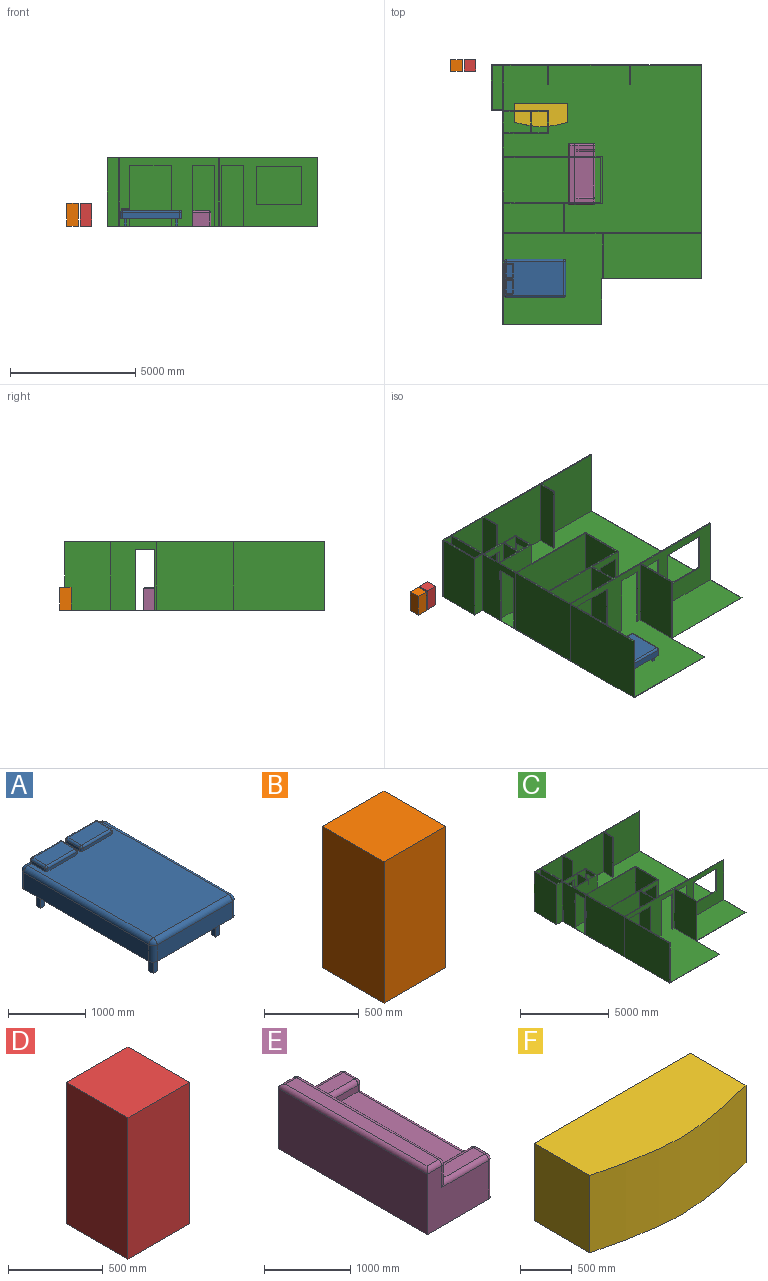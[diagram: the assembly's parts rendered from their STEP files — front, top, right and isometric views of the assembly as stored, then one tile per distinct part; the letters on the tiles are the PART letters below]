
ASSEMBLY  parts=6 mates=7
PART A: 74 faces, bbox 1524x2438.4x716.3 mm
  f0: plane 2286x1371.6mm, normal (0,0,1), area 2817151mm2, adj f9,f10,f14,f15,f39,f40,f42,f46
  f1: plane 1371.6x259.08mm, normal (0,1,0), area 355354.1mm2, adj f5,f8,f14,f17
  f2: plane 2286x259.08mm, normal (-1,0,0), area 592256.9mm2, adj f5,f11,f15,f17
  f3: plane 1371.6x259.08mm, normal (0,-1,0), area 355354.1mm2, adj f5,f6,f10,f11
  f4: plane 2286x259.08mm, normal (1,0,0), area 592256.9mm2, adj f5,f6,f8,f9
  f5: plane 2438.4x1524mm, normal (0,0,-1), area 3687911.5mm2, adj f1,f2,f3,f4,f6,f8,f11,f17
  f6: cylinder r=76.2mm len=259.08mm, axis (0,0,1), area 31010.5mm2, adj f3,f4,f5,f7
  f7: sphere r=76.2mm, area 9120.7mm2, adj f6,f9,f10
  f8: cylinder r=76.2mm len=259.08mm, axis (0,0,-1), area 31010.5mm2, adj f1,f4,f5,f12
  f9: cylinder r=76.2mm len=2286mm, axis (0,-1,0), area 273622mm2, adj f0,f4,f7,f12
  f10: cylinder r=76.2mm len=1371.6mm, axis (-1,0,0), area 164173.2mm2, adj f0,f3,f7,f13
  f11: cylinder r=76.2mm len=259.08mm, axis (0,0,-1), area 31010.5mm2, adj f2,f3,f5,f13
  f12: sphere r=76.2mm, area 9120.7mm2, adj f8,f9,f14
  f13: sphere r=76.2mm, area 9120.7mm2, adj f10,f11,f15
  f14: cylinder r=76.2mm len=1371.6mm, axis (1,0,0), area 164173.2mm2, adj f0,f1,f12,f16,f38,f44
  f15: cylinder r=76.2mm len=2286mm, axis (0,1,0), area 273622mm2, adj f0,f2,f13,f16
  f16: sphere r=76.2mm, area 9120.7mm2, adj f14,f15,f17
  f17: cylinder r=76.2mm len=259.08mm, axis (0,0,1), area 31010.5mm2, adj f1,f2,f5,f16
  f18: plane 304.8x76.2mm, normal (0,-1,0), area 23225.8mm2, adj f5,f19,f21,f22
  f19: plane 304.8x76.2mm, normal (-1,0,0), area 23225.8mm2, adj f5,f18,f20,f22
  f20: plane 304.8x76.2mm, normal (0,1,0), area 23225.8mm2, adj f5,f19,f21,f22
  f21: plane 304.8x76.2mm, normal (1,0,0), area 23225.8mm2, adj f5,f18,f20,f22
  f22: plane 76.2x76.2mm, normal (0,0,-1), area 5806.4mm2, adj f18,f19,f20,f21
  f23: plane 304.8x76.2mm, normal (0,-1,0), area 23225.8mm2, adj f5,f24,f26,f27
  f24: plane 304.8x76.2mm, normal (-1,0,0), area 23225.8mm2, adj f5,f23,f25,f27
  f25: plane 304.8x76.2mm, normal (0,1,0), area 23225.8mm2, adj f5,f24,f26,f27
  f26: plane 304.8x76.2mm, normal (1,0,0), area 23225.8mm2, adj f5,f23,f25,f27
  f27: plane 76.2x76.2mm, normal (0,0,-1), area 5806.4mm2, adj f23,f24,f25,f26
  f28: plane 304.8x76.2mm, normal (1,0,0), area 23225.8mm2, adj f5,f29,f31,f32
  f29: plane 304.8x76.2mm, normal (0,-1,0), area 23225.8mm2, adj f5,f28,f30,f32
  f30: plane 304.8x76.2mm, normal (-1,0,0), area 23225.8mm2, adj f5,f29,f31,f32
  f31: plane 304.8x76.2mm, normal (0,1,0), area 23225.8mm2, adj f5,f28,f30,f32
  f32: plane 76.2x76.2mm, normal (0,0,-1), area 5806.4mm2, adj f28,f29,f30,f31
  f33: plane 304.8x76.2mm, normal (0,-1,0), area 23225.8mm2, adj f5,f34,f36,f37
  f34: plane 304.8x76.2mm, normal (-1,0,0), area 23225.8mm2, adj f5,f33,f35,f37
  f35: plane 304.8x76.2mm, normal (0,1,0), area 23225.8mm2, adj f5,f34,f36,f37
  f36: plane 304.8x76.2mm, normal (1,0,0), area 23225.8mm2, adj f5,f33,f35,f37
  f37: plane 76.2x76.2mm, normal (0,0,-1), area 5806.4mm2, adj f33,f34,f35,f36
  f38: plane 579.07x29.28mm, normal (0,0,-1), area 16555mm2, adj f14,f41,f62,f67
  f39: plane 518.16x45.72mm, normal (0,-1,0), area 23690.3mm2, adj f0,f64,f70,f73
  f40: plane 243.84x45.72mm, normal (1,0,0), area 11148.4mm2, adj f0,f67,f71,f73
  f41: plane 518.16x45.72mm, normal (0,1,0), area 23690.3mm2, adj f38,f62,f66,f67
  f42: plane 243.84x45.72mm, normal (-1,0,0), area 11148.4mm2, adj f0,f62,f64,f65
  f43: plane 518.16x243.84mm, normal (0,0,1), area 126348.1mm2, adj f65,f66,f70,f71
  f44: plane 579.07x29.28mm, normal (0,0,-1), area 16555mm2, adj f14,f45,f52,f61
  f45: plane 518.16x45.72mm, normal (0,1,0), area 23690.3mm2, adj f44,f52,f58,f61
  f46: plane 243.84x45.72mm, normal (-1,0,0), area 11148.4mm2, adj f0,f55,f59,f61
  f47: plane 518.16x45.72mm, normal (0,-1,0), area 23690.3mm2, adj f0,f50,f54,f55
  f48: plane 243.84x45.72mm, normal (1,0,0), area 11148.4mm2, adj f0,f50,f52,f53
  f49: plane 518.16x243.84mm, normal (0,0,1), area 126348.1mm2, adj f53,f54,f58,f59
  f50: cylinder r=30.48mm len=45.72mm, axis (0,0,1), area 2189mm2, adj f0,f47,f48,f51
  f51: sphere r=30.48mm, area 1459.3mm2, adj f50,f53,f54
  f52: cylinder r=30.48mm len=45.72mm, axis (0,0,-1), area 2189mm2, adj f0,f44,f45,f48,f56
  f53: cylinder r=30.48mm len=243.84mm, axis (0,-1,0), area 11674.5mm2, adj f48,f49,f51,f56
  f54: cylinder r=30.48mm len=518.16mm, axis (-1,0,0), area 24808.4mm2, adj f47,f49,f51,f57
  f55: cylinder r=30.48mm len=45.72mm, axis (0,0,-1), area 2189mm2, adj f0,f46,f47,f57
  f56: sphere r=30.48mm, area 1459.3mm2, adj f52,f53,f58
  f57: sphere r=30.48mm, area 1459.3mm2, adj f54,f55,f59
  f58: cylinder r=30.48mm len=518.16mm, axis (1,0,0), area 24808.4mm2, adj f45,f49,f56,f60
  f59: cylinder r=30.48mm len=243.84mm, axis (0,1,0), area 11674.5mm2, adj f46,f49,f57,f60
  f60: sphere r=30.48mm, area 1459.3mm2, adj f58,f59,f61
  f61: cylinder r=30.48mm len=45.72mm, axis (0,0,1), area 2189mm2, adj f0,f44,f45,f46,f60
  f62: cylinder r=30.48mm len=45.72mm, axis (0,0,1), area 2189mm2, adj f0,f38,f41,f42,f63
  f63: sphere r=30.48mm, area 1459.3mm2, adj f62,f65,f66
  f64: cylinder r=30.48mm len=45.72mm, axis (0,0,-1), area 2189mm2, adj f0,f39,f42,f68
  f65: cylinder r=30.48mm len=243.84mm, axis (0,1,0), area 11674.5mm2, adj f42,f43,f63,f68
  f66: cylinder r=30.48mm len=518.16mm, axis (1,0,0), area 24808.4mm2, adj f41,f43,f63,f69
  f67: cylinder r=30.48mm len=45.72mm, axis (0,0,-1), area 2189mm2, adj f0,f38,f40,f41,f69
  f68: sphere r=30.48mm, area 1459.3mm2, adj f64,f65,f70
  f69: sphere r=30.48mm, area 1459.3mm2, adj f66,f67,f71
  f70: cylinder r=30.48mm len=518.16mm, axis (-1,0,0), area 24808.4mm2, adj f39,f43,f68,f72
  f71: cylinder r=30.48mm len=243.84mm, axis (0,-1,0), area 11674.5mm2, adj f40,f43,f69,f72
  f72: sphere r=30.48mm, area 1459.3mm2, adj f70,f71,f73
  f73: cylinder r=30.48mm len=45.72mm, axis (0,0,1), area 2189mm2, adj f0,f39,f40,f72
PART B: 6 faces, bbox 457.2x457.2x914.4 mm
  f0: plane 914.4x457.2mm, normal (0,-1,0), area 418063.7mm2, adj f1,f3,f4,f5
  f1: plane 914.4x457.2mm, normal (1,0,0), area 418063.7mm2, adj f0,f2,f4,f5
  f2: plane 914.4x457.2mm, normal (0,1,0), area 418063.7mm2, adj f1,f3,f4,f5
  f3: plane 914.4x457.2mm, normal (-1,0,0), area 418063.7mm2, adj f0,f2,f4,f5
  f4: plane 457.2x457.2mm, normal (0,0,1), area 209031.8mm2, adj f0,f1,f2,f3
  f5: plane 457.2x457.2mm, normal (0,0,-1), area 209031.8mm2, adj f0,f1,f2,f3
PART C: 85 faces, bbox 8382x10363.2x2750.8 mm
  f0: plane 3915.35x2743.2mm, normal (0,-1,0), area 5798149.8mm2, adj f2,f10,f19,f23,f78,f79,f80,f81
  f1: plane 3093.72x1.33mm, normal (0,0,1), area 4110.8mm2, adj f14,f17,f71,f73
  f2: plane 10324.82x7924.8mm, normal (0,0,1), area 73158988.7mm2, adj f0,f3,f4,f5,f6,f7,f8,f9
  f3: plane 3918.01x2743.2mm, normal (0,1,0), area 10747881.6mm2, adj f2,f16,f23,f72
  f4: plane 2743.2x1790.42mm, normal (1,0,0), area 4911492.8mm2, adj f2,f5,f23,f62
  f5: plane 2743.2x1783.08mm, normal (0,1,0), area 3033284.3mm2, adj f2,f4,f23,f42,f54,f55,f56
  f6: plane 3918.01x2743.2mm, normal (0,-1,0), area 4504797.3mm2, adj f2,f18,f23,f35,f36,f37,f38,f39
  f7: plane 3962.4x2750.82mm, normal (0,-1,0), area 155612.6mm2, adj f2,f8,f14,f15,f23,f74
  f8: plane 1828.8x7.62mm, normal (1,0,0), area 13935.5mm2, adj f2,f7,f9,f15
  f9: plane 3962.4x2750.82mm, normal (0,-1,0), area 155612.6mm2, adj f2,f8,f10,f15,f18,f19,f23
  f10: plane 8534.4x2750.82mm, normal (1,0,0), area 295722.6mm2, adj f0,f2,f9,f11,f15,f20,f23,f70
  f11: plane 8382x2750.82mm, normal (0,1,0), area 23057373.2mm2, adj f10,f12,f15,f23
  f12: plane 2750.82x1828.8mm, normal (-1,0,0), area 5030699.6mm2, adj f11,f13,f15,f23
  f13: plane 2750.82x457.2mm, normal (0,-1,0), area 1257674.9mm2, adj f12,f14,f15,f23
  f14: plane 8534.4x2750.82mm, normal (-1,0,0), area 13131844.7mm2, adj f1,f2,f7,f13,f15,f23,f71,f73
  f15: plane 10363.2x8382mm, normal (0,0,-1), area 75715977.6mm2, adj f7,f8,f9,f10,f11,f12,f13,f14
  f16: plane 2743.2x1874.52mm, normal (1,0,0), area 5142183.3mm2, adj f2,f3,f22,f23
  f17: plane 3093.72x2743.2mm, normal (-1,0,0), area 8486692.7mm2, adj f1,f23,f71,f73
  f18: plane 2743.2x1783.08mm, normal (-1,0,0), area 4891345.1mm2, adj f2,f6,f9,f23
  f19: plane 2743.2x1783.08mm, normal (1,0,0), area 4891345.1mm2, adj f0,f2,f9,f23
  f20: plane 5439.35x2743.2mm, normal (0,1,0), area 7823436.1mm2, adj f2,f10,f21,f23,f35,f36,f37,f78
  f21: plane 2743.2x1173.48mm, normal (1,0,0), area 3219090.3mm2, adj f2,f20,f22,f23
  f22: plane 2743.2x1478.28mm, normal (0,-1,0), area 1899867.2mm2, adj f2,f16,f21,f23,f32,f33,f34
  f23: plane 10363.2x8382mm, normal (0,0,1), area 2140388.6mm2, adj f0,f3,f4,f5,f6,f7,f9,f10
  f24: plane 2743.2x2392.68mm, normal (0,1,0), area 2475866mm2, adj f2,f23,f25,f27,f38,f39,f40
  f25: plane 2743.2x1173.48mm, normal (-1,0,0), area 3219090.3mm2, adj f2,f23,f24,f26
  f26: plane 2743.2x2392.68mm, normal (0,-1,0), area 6563599.8mm2, adj f2,f23,f25,f27
  f27: plane 2743.2x1173.48mm, normal (1,0,0), area 3219090.3mm2, adj f2,f23,f24,f26
  f28: plane 3870.96x2743.2mm, normal (0,1,0), area 8463466.9mm2, adj f2,f23,f29,f31,f32,f33,f34
  f29: plane 2743.2x1783.08mm, normal (-1,0,0), area 4891345.1mm2, adj f2,f23,f28,f30
  f30: plane 3870.96x2743.2mm, normal (0,-1,0), area 10618817.5mm2, adj f2,f23,f29,f31
  f31: plane 2743.2x1783.08mm, normal (1,0,0), area 4891345.1mm2, adj f2,f23,f28,f30
  f32: plane 2438.4x45.72mm, normal (1,0,0), area 111483.6mm2, adj f2,f22,f28,f34
  f33: plane 2438.4x45.72mm, normal (-1,0,0), area 111483.6mm2, adj f2,f22,f28,f34
  f34: plane 883.92x45.72mm, normal (0,0,-1), area 40412.8mm2, adj f22,f28,f32,f33
  f35: plane 883.92x45.72mm, normal (0,0,-1), area 40412.8mm2, adj f6,f20,f36,f37
  f36: plane 2438.4x45.72mm, normal (1,0,0), area 111483.6mm2, adj f2,f6,f20,f35
  f37: plane 2438.4x45.72mm, normal (-1,0,0), area 111483.6mm2, adj f2,f6,f20,f35
  f38: plane 2438.4x45.72mm, normal (-1,0,0), area 111483.6mm2, adj f2,f6,f24,f39
  f39: plane 1676.4x45.72mm, normal (0,0,-1), area 76645mm2, adj f6,f24,f38,f40
  f40: plane 2438.4x45.72mm, normal (1,0,0), area 111483.6mm2, adj f2,f6,f24,f39
  f41: plane 2743.2x1783.08mm, normal (0,-1,0), area 4891345.1mm2, adj f2,f23,f42,f72
  f42: plane 2743.2x914.4mm, normal (1,0,0), area 650321.3mm2, adj f2,f5,f23,f41,f51,f52,f53
  f43: plane 2743.2x1066.8mm, normal (0,1,0), area 2926445.8mm2, adj f2,f23,f44,f46
  f44: plane 2743.2x822.96mm, normal (-1,0,0), area 2257543.9mm2, adj f2,f23,f43,f45
  f45: plane 2743.2x1066.8mm, normal (0,-1,0), area 1068385mm2, adj f2,f23,f44,f46,f54,f55,f56
  f46: plane 2743.2x822.96mm, normal (1,0,0), area 2257543.9mm2, adj f2,f23,f43,f45
  f47: plane 2743.2x624.84mm, normal (0,1,0), area 1714061.1mm2, adj f2,f23,f48,f50
  f48: plane 2743.2x822.96mm, normal (-1,0,0), area 399483.1mm2, adj f2,f23,f47,f49,f51,f52,f53
  f49: plane 2743.2x624.84mm, normal (0,-1,0), area 1714061.1mm2, adj f2,f23,f48,f50
  f50: plane 2743.2x822.96mm, normal (1,0,0), area 2257543.9mm2, adj f2,f23,f47,f49
  f51: plane 2438.4x45.72mm, normal (0,-1,0), area 111483.6mm2, adj f2,f42,f48,f52
  f52: plane 762x45.72mm, normal (0,0,-1), area 34838.6mm2, adj f42,f48,f51,f53
  f53: plane 2438.4x45.72mm, normal (0,1,0), area 111483.6mm2, adj f2,f42,f48,f52
  f54: plane 762x45.72mm, normal (0,0,-1), area 34838.6mm2, adj f5,f45,f55,f56
  f55: plane 2438.4x45.72mm, normal (-1,0,0), area 111483.6mm2, adj f2,f5,f45,f54
  f56: plane 2438.4x45.72mm, normal (1,0,0), area 111483.6mm2, adj f2,f5,f45,f54
  f57: plane 2743.2x411.48mm, normal (0,1,0), area 1128771.9mm2, adj f23,f58,f60,f61
  f58: plane 2743.2x1737.36mm, normal (-1,0,0), area 4765926mm2, adj f23,f57,f59,f61
  f59: plane 2743.2x411.48mm, normal (0,-1,0), area 1128771.9mm2, adj f23,f58,f60,f61
  f60: plane 2743.2x1737.36mm, normal (1,0,0), area 4765926mm2, adj f23,f57,f59,f61
  f61: plane 1737.36x411.48mm, normal (0,0,1), area 714888.9mm2, adj f57,f58,f59,f60
  f62: plane 2743.2x1752.6mm, normal (0,-1,0), area 4807732.3mm2, adj f2,f4,f23,f63
  f63: plane 2743.2x762mm, normal (-1,0,0), area 2090318.4mm2, adj f2,f23,f62,f64
  f64: plane 2743.2x45.72mm, normal (0,-1,0), area 125419.1mm2, adj f2,f23,f63,f65
  f65: plane 2743.2x762mm, normal (1,0,0), area 2090318.4mm2, adj f2,f23,f64,f66
  f66: plane 3200.4x2743.2mm, normal (0,-1,0), area 8779337.3mm2, adj f2,f23,f65,f67
  f67: plane 2743.2x762mm, normal (-1,0,0), area 2090318.4mm2, adj f2,f23,f66,f68
  f68: plane 2743.2x45.72mm, normal (0,-1,0), area 125419.1mm2, adj f2,f23,f67,f69
  f69: plane 2743.2x762mm, normal (1,0,0), area 2090318.4mm2, adj f2,f23,f68,f70
  f70: plane 2834.64x2743.2mm, normal (0,-1,0), area 7775984.4mm2, adj f2,f10,f23,f69
  f71: plane 2743.2x1.33mm, normal (0,-1,0), area 3645mm2, adj f1,f14,f17,f23
  f72: plane 2743.2x914.4mm, normal (1,0,0), area 650321.3mm2, adj f2,f3,f23,f41,f75,f76,f77
  f73: plane 2743.2x1.33mm, normal (0,1,0), area 3645mm2, adj f1,f14,f17,f23
  f74: plane 3611.88x2743.2mm, normal (1,0,0), area 9908109.2mm2, adj f2,f6,f7,f23
  f75: plane 2438.4x45.72mm, normal (0,1,0), area 111483.6mm2, adj f2,f14,f72,f76
  f76: plane 762x45.72mm, normal (0,0,-1), area 34838.6mm2, adj f14,f72,f75,f77
  f77: plane 2438.4x45.72mm, normal (0,-1,0), area 111483.6mm2, adj f2,f14,f72,f76
  f78: plane 2438.4x45.72mm, normal (-1,0,0), area 111483.6mm2, adj f0,f2,f20,f79
  f79: plane 883.92x45.72mm, normal (0,0,-1), area 40412.8mm2, adj f0,f20,f78,f80
  f80: plane 2438.4x45.72mm, normal (1,0,0), area 111483.6mm2, adj f0,f2,f20,f79
  f81: plane 1828.8x45.72mm, normal (0,0,1), area 83612.7mm2, adj f0,f20,f82,f84
  f82: plane 1524x45.72mm, normal (-1,0,0), area 69677.3mm2, adj f0,f20,f81,f83
  f83: plane 1828.8x45.72mm, normal (0,0,-1), area 83612.7mm2, adj f0,f20,f82,f84
  f84: plane 1524x45.72mm, normal (1,0,0), area 69677.3mm2, adj f0,f20,f81,f83
PART D: 6 faces, bbox 457.2x457.2x914.4 mm
  f0: plane 914.4x457.2mm, normal (0,-1,0), area 418063.7mm2, adj f1,f3,f4,f5
  f1: plane 914.4x457.2mm, normal (1,0,0), area 418063.7mm2, adj f0,f2,f4,f5
  f2: plane 914.4x457.2mm, normal (0,1,0), area 418063.7mm2, adj f1,f3,f4,f5
  f3: plane 914.4x457.2mm, normal (-1,0,0), area 418063.7mm2, adj f0,f2,f4,f5
  f4: plane 457.2x457.2mm, normal (0,0,1), area 209031.8mm2, adj f0,f1,f2,f3
  f5: plane 457.2x457.2mm, normal (0,0,-1), area 209031.8mm2, adj f0,f1,f2,f3
PART E: 35 faces, bbox 1066.8x2438.4x914.4 mm
  f0: plane 2316.48x548.64mm, normal (1,0,0), area 973623.9mm2, adj f6,f14,f15,f16,f17,f20,f25,f26
  f1: plane 2316.48x182.88mm, normal (0,0,1), area 423637.9mm2, adj f23,f27,f30,f31
  f2: plane 1005.84x853.44mm, normal (0,1,0), area 626166.5mm2, adj f4,f6,f15,f21,f23,f24
  f3: plane 701.04x91.44mm, normal (0,-1,0), area 64103.1mm2, adj f8,f9,f12,f14
  f4: plane 2438.4x853.44mm, normal (-1,0,0), area 2081028.1mm2, adj f2,f5,f6,f27
  f5: plane 1005.84x853.44mm, normal (0,-1,0), area 626166.5mm2, adj f4,f6,f26,f30,f32,f34
  f6: plane 2438.4x1066.8mm, normal (0,0,-1), area 2599690.1mm2, adj f0,f2,f4,f5,f15,f26
  f7: plane 701.04x91.44mm, normal (0,1,0), area 64103.1mm2, adj f8,f9,f19,f20
  f8: plane 2316.48x396.24mm, normal (1,0,0), area 845154.6mm2, adj f3,f7,f9,f10,f11,f12,f19,f24
  f9: plane 1828.8x701.04mm, normal (0,0,1), area 1282062mm2, adj f3,f7,f8,f17
  f10: plane 701.04x182.88mm, normal (0,0,1), area 128206.2mm2, adj f8,f12,f16,f21
  f11: plane 701.04x182.88mm, normal (0,0,1), area 128206.2mm2, adj f8,f19,f25,f32
  f12: cylinder r=60.96mm len=701.04mm, axis (1,0,0), area 67128.6mm2, adj f3,f8,f10,f13
  f13: sphere r=60.96mm, area 5837.3mm2, adj f12,f14,f16
  f14: cylinder r=60.96mm len=152.4mm, axis (0,0,1), area 10877.1mm2, adj f0,f3,f13,f17
  f15: cylinder r=60.96mm len=548.64mm, axis (0,0,-1), area 52535.4mm2, adj f0,f2,f6,f18
  f16: cylinder r=60.96mm len=182.88mm, axis (0,-1,0), area 17511.8mm2, adj f0,f10,f13,f18
  f17: cylinder r=60.96mm len=1950.72mm, axis (0,-1,0), area 179360.4mm2, adj f0,f9,f14,f20
  f18: sphere r=60.96mm, area 5837.3mm2, adj f15,f16,f21
  f19: cylinder r=60.96mm len=701.04mm, axis (-1,0,0), area 67128.6mm2, adj f7,f8,f11,f22
  f20: cylinder r=60.96mm len=152.4mm, axis (0,0,-1), area 10877.1mm2, adj f0,f7,f17,f22
  f21: cylinder r=60.96mm len=762mm, axis (1,0,0), area 69249.8mm2, adj f2,f10,f18,f24
  f22: sphere r=60.96mm, area 5837.3mm2, adj f19,f20,f25
  f23: cylinder r=60.96mm len=243.84mm, axis (1,0,0), area 21227.9mm2, adj f1,f2,f27,f28
  f24: cylinder r=60.96mm len=304.8mm, axis (0,0,-1), area 25470.2mm2, adj f2,f8,f21,f28
  f25: cylinder r=60.96mm len=182.88mm, axis (0,-1,0), area 17511.8mm2, adj f0,f11,f22,f29
  f26: cylinder r=60.96mm len=548.64mm, axis (0,0,1), area 52535.4mm2, adj f0,f5,f6,f29
  f27: cylinder r=60.96mm len=2438.4mm, axis (0,1,0), area 229248.5mm2, adj f1,f4,f23,f30
  f28: sphere r=60.96mm, area 5837.3mm2, adj f23,f24,f31
  f29: sphere r=60.96mm, area 5837.3mm2, adj f25,f26,f32
  f30: cylinder r=60.96mm len=243.84mm, axis (-1,0,0), area 21227.9mm2, adj f1,f5,f27,f33
  f31: cylinder r=60.96mm len=2316.48mm, axis (0,1,0), area 221816.3mm2, adj f1,f8,f28,f33
  f32: cylinder r=60.96mm len=762mm, axis (-1,0,0), area 69249.8mm2, adj f5,f11,f29,f34
  f33: sphere r=60.96mm, area 5837.3mm2, adj f30,f31,f34
  f34: cylinder r=60.96mm len=304.8mm, axis (0,0,1), area 25470.2mm2, adj f5,f8,f32,f33
PART F: 6 faces, bbox 2133.6x945.7x914.4 mm
  f0: extruded ~2133.6x914.4mm, area 1981940.1mm2, adj f1,f3,f4,f5
  f1: plane 914.4x762mm, normal (1,0,0), area 696772.8mm2, adj f0,f2,f4,f5
  f2: plane 2133.6x914.4mm, normal (0,1,0), area 1950963.8mm2, adj f1,f3,f4,f5
  f3: plane 914.4x762mm, normal (-1,0,0), area 696772.8mm2, adj f0,f2,f4,f5
  f4: plane 2133.6x945.68mm, normal (0,0,1), area 1858528.2mm2, adj f0,f1,f2,f3
  f5: plane 2133.6x945.68mm, normal (0,0,-1), area 1858528.2mm2, adj f0,f1,f2,f3
PLACE A rot(axis=(0,0,1),90deg) t=(-188.72,-2487.79,796.69)mm
PLACE B t=(-318.91,-535.15,491.89)mm
PLACE C t=(2177.55,-804.17,491.89)mm
PLACE D t=(-377.86,-536.59,491.89)mm
PLACE E t=(1362.73,1181.18,491.89)mm
PLACE F t=(-238.04,-368,491.89)mm
MATE parallel F.f2 <-> C.f5  axis (0,1,0) through (-246.92,4505.25,949.09)mm
MATE parallel F.f1 <-> C.f67  axis (1,0,0) through (819.88,4124.25,949.09)mm
MATE planar B.f5 <-> C.f2  axis (0,0,-1) through (-3631.52,6018.7,491.89)mm
MATE planar F.f5 <-> C.f2  axis (0,0,-1) through (-246.75,4068.07,491.89)mm
MATE planar A.f22 <-> C.f2  axis (0,0,-1) through (533.88,-3059.61,491.89)mm
MATE planar D.f5 <-> C.f2  axis (0,0,-1) through (-3084.36,6017.26,491.89)mm
MATE planar E.f6 <-> C.f2  axis (0,0,-1) through (1363.58,1667.41,491.89)mm
